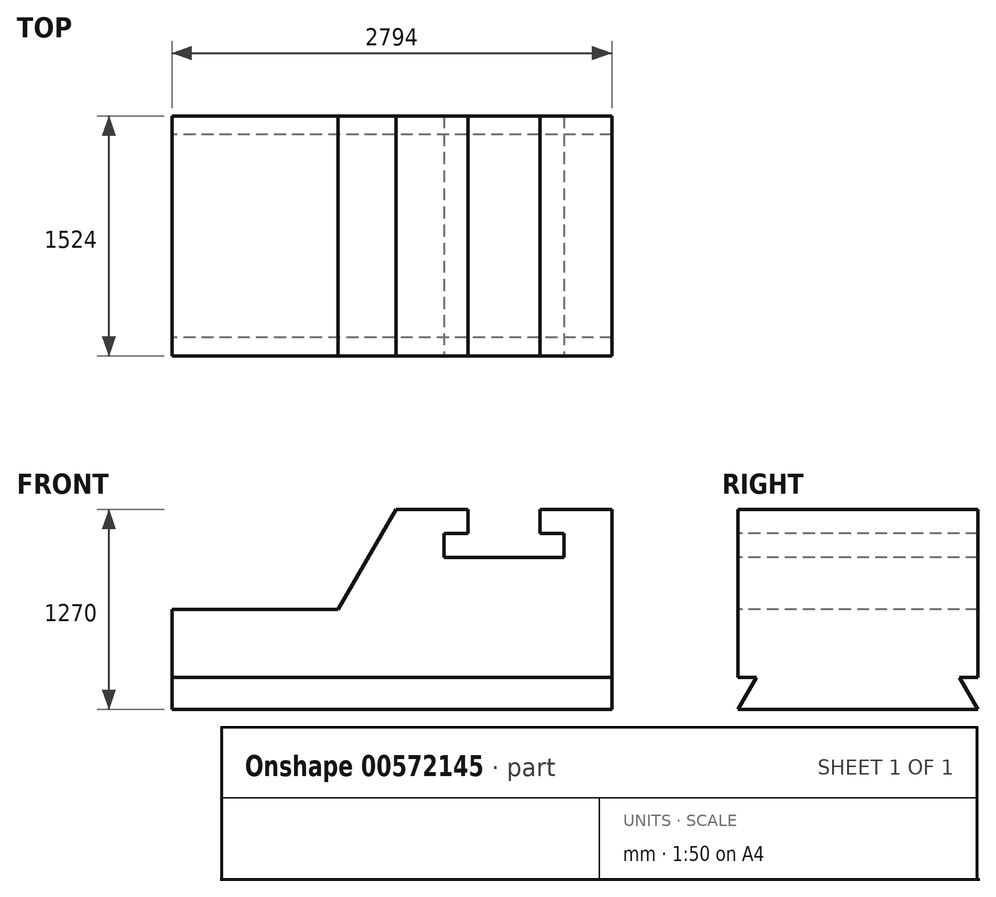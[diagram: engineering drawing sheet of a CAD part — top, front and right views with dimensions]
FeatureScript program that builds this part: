
annotation { "Feature Type Name" : "Feature", "Feature Type Description" : "" }
export const myFeature = defineFeature(function(context is Context, id is Id, definition is map)
    precondition{}
    {
        {
            var Q0;
            Q0=qCreatedBy(makeId("Front.planeOp"),FACE);
            var sketch = newSketch(context, id + "F0", { "sketchPlane" : qUnion([Q0])});
            skLineSegment(sketch, "E0.bottom", {"start": v(0, 0) * mm, "end": v(2794, 0) * mm});
            skLineSegment(sketch, "E0.top", {"start": v(0, 1270) * mm, "end": v(2794, 1270) * mm});
            skLineSegment(sketch, "E0.left", {"start": v(0, 0) * mm, "end": v(0, 1270) * mm});
            skLineSegment(sketch, "E0.right", {"start": v(2794, 0) * mm, "end": v(2794, 1270) * mm});
            skSolve(sketch);
        }
        {
            var Q0;
            Q0=makeQuery(id+"F0.imprint","IMPRINT",FACE,{"disambiguationData":[TD([[makeQuery(id+"F0.imprint","IMPRINT",EDGE,{"derivedFrom":sQuery(id+"F0.wireOp",EDGE,"E0.bottom")}),1.0]])]});
            extrude(context, id + "F1", {"entities" : qUnion([Q0]), "depth" : 1524 * mm, "offsetDistance" : 25.4 * mm});
        }
        {
            var Q0;
            Q0=makeQuery(id+"F1.opExtrude","CAP_FACE",FACE,{"disambiguationData":[OSD([sQuery(id+"F0.wireOp",EDGE,"E0.bottom"),sQuery(id+"F0.wireOp",EDGE,"E0.top"),sQuery(id+"F0.wireOp",EDGE,"E0.left"),sQuery(id+"F0.wireOp",EDGE,"E0.right")])],"isStart":false});
            var sketch = newSketch(context, id + "F2", { "sketchPlane" : qUnion([Q0])});
            skLineSegment(sketch, "E1", {"start": v(2794, 1270) * mm, "end": v(1422.4, 1270) * mm});
            skLineSegment(sketch, "E2", {"start": v(0, 635) * mm, "end": v(1055.78, 635) * mm});
            skLineSegment(sketch, "E3", {"start": v(1055.78, 635) * mm, "end": v(1422.4, 1270) * mm});
            skSolve(sketch);
        }
        {
            var Q0;
            {var subQ0=sQuery(id+"F2.wireOp",EDGE,"E2");Q0=makeQuery(id+"F2.imprint","IMPRINT",FACE,{"disambiguationData":[TD([[makeQuery(id+"F2.imprint","IMPRINT",EDGE,{"derivedFrom":subQ0}),1.0]])]});}
            extrude(context, id + "F3", {"entities" : qUnion([Q0]), "operationType" : NewBodyOperationType.REMOVE, "endBound" : BoundingType.THROUGH_ALL, "oppositeDirection" : true, "depth" : 25.4 * mm, "offsetDistance" : 25.4 * mm});
        }
        {
            var Q0;
            Q0=makeQuery(id+"F1.opExtrude","CAP_FACE",FACE,{"disambiguationData":[OSD([sQuery(id+"F0.wireOp",EDGE,"E0.bottom"),sQuery(id+"F0.wireOp",EDGE,"E0.top"),sQuery(id+"F0.wireOp",EDGE,"E0.left"),sQuery(id+"F0.wireOp",EDGE,"E0.right")])],"isStart":false});
            var sketch = newSketch(context, id + "F4", { "sketchPlane" : qUnion([Q0])});
            skLineSegment(sketch, "E4", {"start": v(2794, 1270) * mm, "end": v(2336.8, 1270) * mm});
            skLineSegment(sketch, "E5", {"start": v(2336.8, 1270) * mm, "end": v(1879.6, 1270) * mm});
            skLineSegment(sketch, "E6", {"start": v(1879.6, 1270) * mm, "end": v(1422.4, 1270) * mm});
            skLineSegment(sketch, "E7", {"start": v(1879.6, 1270) * mm, "end": v(1879.6, 1117.6) * mm});
            skLineSegment(sketch, "E8", {"start": v(1879.6, 1117.6) * mm, "end": v(1727.2, 1117.6) * mm});
            skLineSegment(sketch, "E9", {"start": v(1727.2, 1117.6) * mm, "end": v(1727.2, 965.2) * mm});
            skLineSegment(sketch, "E10", {"start": v(1727.2, 965.2) * mm, "end": v(2489.2, 965.2) * mm});
            skLineSegment(sketch, "E11", {"start": v(2489.2, 965.2) * mm, "end": v(2489.2, 1117.6) * mm});
            skLineSegment(sketch, "E12", {"start": v(2489.2, 1117.6) * mm, "end": v(2336.8, 1117.6) * mm});
            skLineSegment(sketch, "E13", {"start": v(2336.8, 1117.6) * mm, "end": v(2336.8, 1270) * mm});
            skSolve(sketch);
        }
        {
            var Q0;
            Q0=makeQuery(id+"F4.imprint","IMPRINT",FACE,{"disambiguationData":[TD([[makeQuery(id+"F4.imprint","IMPRINT",EDGE,{"derivedFrom":sQuery(id+"F4.wireOp",EDGE,"E5")}),-1.0]])]});
            extrude(context, id + "F5", {"entities" : qUnion([Q0]), "operationType" : NewBodyOperationType.REMOVE, "endBound" : BoundingType.THROUGH_ALL, "oppositeDirection" : true, "depth" : 25.4 * mm, "offsetDistance" : 25.4 * mm});
        }
        {
            var Q0;
            Q0=makeQuery(id+"F1.opExtrude","SWEPT_FACE",FACE,{"disambiguationData":[OSD([sQuery(id+"F0.wireOp",EDGE,"E0.left")])]});
            var sketch = newSketch(context, id + "F6", { "sketchPlane" : qUnion([Q0])});
            skLineSegment(sketch, "E14", {"start": v(1524, 0) * mm, "end": v(1524, 203.2) * mm});
            skLineSegment(sketch, "E15", {"start": v(1524, 203.2) * mm, "end": v(1406.68, 203.2) * mm});
            skLineSegment(sketch, "E16", {"start": v(1406.68, 203.2) * mm, "end": v(1524, 0) * mm});
            skSolve(sketch);
        }
        {
            var Q0;
            Q0=makeQuery(id+"F6.imprint","IMPRINT",FACE,{"disambiguationData":[TD([[makeQuery(id+"F6.imprint","IMPRINT",EDGE,{"derivedFrom":sQuery(id+"F6.wireOp",EDGE,"E14")}),1.0]])]});
            extrude(context, id + "F7", {"entities" : qUnion([Q0]), "operationType" : NewBodyOperationType.REMOVE, "endBound" : BoundingType.THROUGH_ALL, "oppositeDirection" : true, "depth" : 25.4 * mm, "offsetDistance" : 25.4 * mm});
        }
        {
            var Q0;
            Q0=makeQuery(id+"F1.opExtrude","SWEPT_FACE",FACE,{"disambiguationData":[OSD([sQuery(id+"F0.wireOp",EDGE,"E0.left")])]});
            var sketch = newSketch(context, id + "F8", { "sketchPlane" : qUnion([Q0])});
            skLineSegment(sketch, "E17", {"start": v(0, 0) * mm, "end": v(0, 203.2) * mm});
            skLineSegment(sketch, "E18", {"start": v(0, 203.2) * mm, "end": v(117.32, 203.2) * mm});
            skLineSegment(sketch, "E19", {"start": v(117.32, 203.2) * mm, "end": v(0, 0) * mm});
            skSolve(sketch);
        }
        {
            var Q0;
            Q0=makeQuery(id+"F8.imprint","IMPRINT",FACE,{"disambiguationData":[TD([[makeQuery(id+"F8.imprint","IMPRINT",EDGE,{"derivedFrom":sQuery(id+"F8.wireOp",EDGE,"E17")}),-1.0]])]});
            extrude(context, id + "F9", {"entities" : qUnion([Q0]), "operationType" : NewBodyOperationType.REMOVE, "endBound" : BoundingType.THROUGH_ALL, "oppositeDirection" : true, "depth" : 25.4 * mm, "offsetDistance" : 25.4 * mm});
        }
    });
